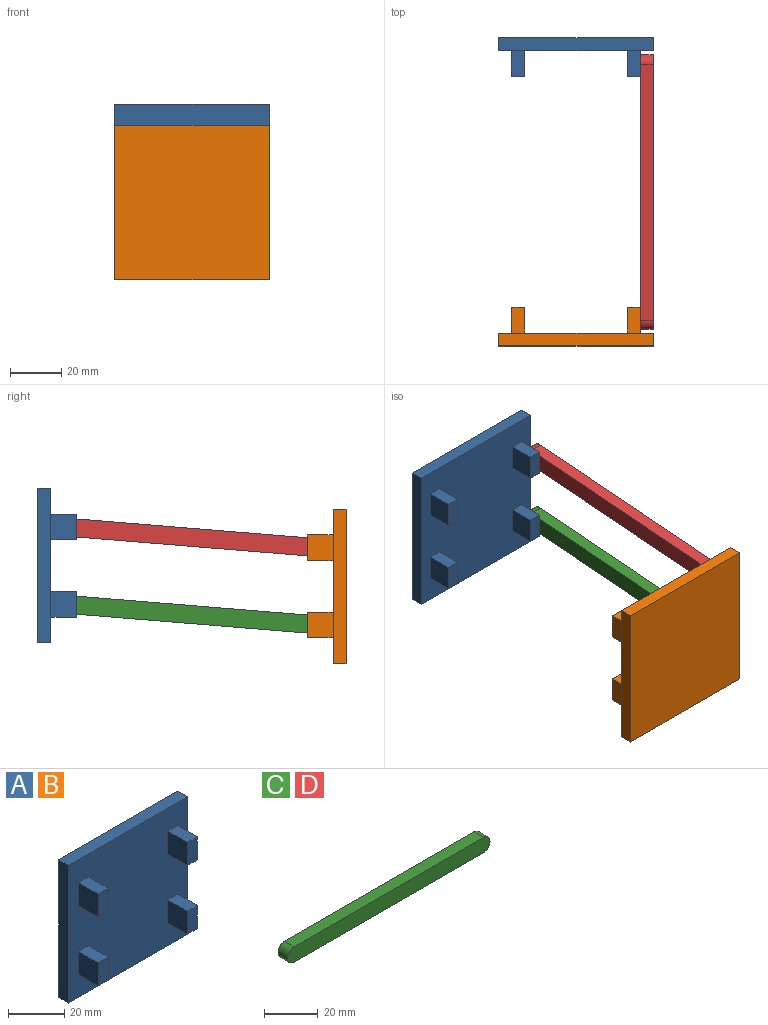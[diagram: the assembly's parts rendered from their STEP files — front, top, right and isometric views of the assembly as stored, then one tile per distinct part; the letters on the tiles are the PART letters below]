
ASSEMBLY  parts=4 mates=4
PART A: 26 faces, bbox 60x15x60 mm
  f0: plane 60x5mm, normal (0,0,1), area 300mm2, adj f1,f3,f4,f5
  f1: plane 60x5mm, normal (-1,0,0), area 300mm2, adj f0,f2,f4,f5
  f2: plane 60x5mm, normal (0,0,-1), area 300mm2, adj f1,f3,f4,f5
  f3: plane 60x5mm, normal (1,0,0), area 300mm2, adj f0,f2,f4,f5
  f4: plane 60x60mm, normal (0,-1,0), area 3400mm2, adj f0,f1,f2,f3,f7,f8,f9,f10
  f5: plane 60x60mm, normal (0,1,0), area 3600mm2, adj f0,f1,f2,f3
  f6: plane 10x5mm, normal (0,-1,0), area 50mm2, adj f7,f8,f9,f10
  f7: plane 10x10mm, normal (1,0,0), area 100mm2, adj f4,f6,f8,f10
  f8: plane 10x5mm, normal (0,0,-1), area 50mm2, adj f4,f6,f7,f9
  f9: plane 10x10mm, normal (-1,0,0), area 100mm2, adj f4,f6,f8,f10
  f10: plane 10x5mm, normal (0,0,1), area 50mm2, adj f4,f6,f7,f9
  f11: plane 10x5mm, normal (0,-1,0), area 50mm2, adj f12,f13,f14,f15
  f12: plane 10x10mm, normal (1,0,0), area 100mm2, adj f4,f11,f13,f15
  f13: plane 10x5mm, normal (0,0,-1), area 50mm2, adj f4,f11,f12,f14
  f14: plane 10x10mm, normal (-1,0,0), area 100mm2, adj f4,f11,f13,f15
  f15: plane 10x5mm, normal (0,0,1), area 50mm2, adj f4,f11,f12,f14
  f16: plane 10x5mm, normal (0,-1,0), area 50mm2, adj f17,f18,f19,f20
  f17: plane 10x5mm, normal (0,0,-1), area 50mm2, adj f4,f16,f18,f20
  f18: plane 10x10mm, normal (-1,0,0), area 100mm2, adj f4,f16,f17,f19
  f19: plane 10x5mm, normal (0,0,1), area 50mm2, adj f4,f16,f18,f20
  f20: plane 10x10mm, normal (1,0,0), area 100mm2, adj f4,f16,f17,f19
  f21: plane 10x5mm, normal (0,-1,0), area 50mm2, adj f22,f23,f24,f25
  f22: plane 10x10mm, normal (-1,0,0), area 100mm2, adj f4,f21,f23,f25
  f23: plane 10x5mm, normal (0,0,1), area 50mm2, adj f4,f21,f22,f24
  f24: plane 10x10mm, normal (1,0,0), area 100mm2, adj f4,f21,f23,f25
  f25: plane 10x5mm, normal (0,0,-1), area 50mm2, adj f4,f21,f22,f24
PART B: same geometry as A
PART C: 6 faces, bbox 107x5x7 mm
  f0: cylinder r=3.5mm len=7mm, axis (0,1,0), area 55mm2, adj f1,f3,f4,f5
  f1: plane 100x5mm, normal (0,0,-1), area 500mm2, adj f0,f2,f4,f5
  f2: cylinder r=3.5mm len=7mm, axis (0,1,0), area 55mm2, adj f1,f3,f4,f5
  f3: plane 100x5mm, normal (0,0,1), area 500mm2, adj f0,f2,f4,f5
  f4: plane 107x7mm, normal (0,-1,0), area 738.5mm2, adj f0,f1,f2,f3
  f5: plane 107x7mm, normal (0,1,0), area 738.5mm2, adj f0,f1,f2,f3
PART D: same geometry as C
PLACE A t=(-10.89,-9.61,-7.65)mm fixed
PLACE B rot(axis=(1,0,0),180deg) t=(-10.89,-129.27,-39.61)mm
PLACE C rot(axis=(-0.71,-0.71,-0.03),176.7deg) t=(-45.66,-80.8,11.33)mm
PLACE D rot(axis=(-0.71,-0.71,-0.03),176.7deg) t=(-45.66,-80.8,41.33)mm
MATE revolute C.f2 <-> A.f20  axis (-1,0,0) through (-50.66,-19.61,-34.57)mm
MATE revolute D.f0 <-> B.f20  axis (-1,0,0) through (-50.66,-119.27,-12.7)mm
MATE revolute C.f0 <-> B.f12  axis (-1,0,0) through (-50.66,-119.27,-42.7)mm
MATE revolute D.f2 <-> A.f12  axis (-1,0,0) through (-50.66,-19.61,-4.57)mm
